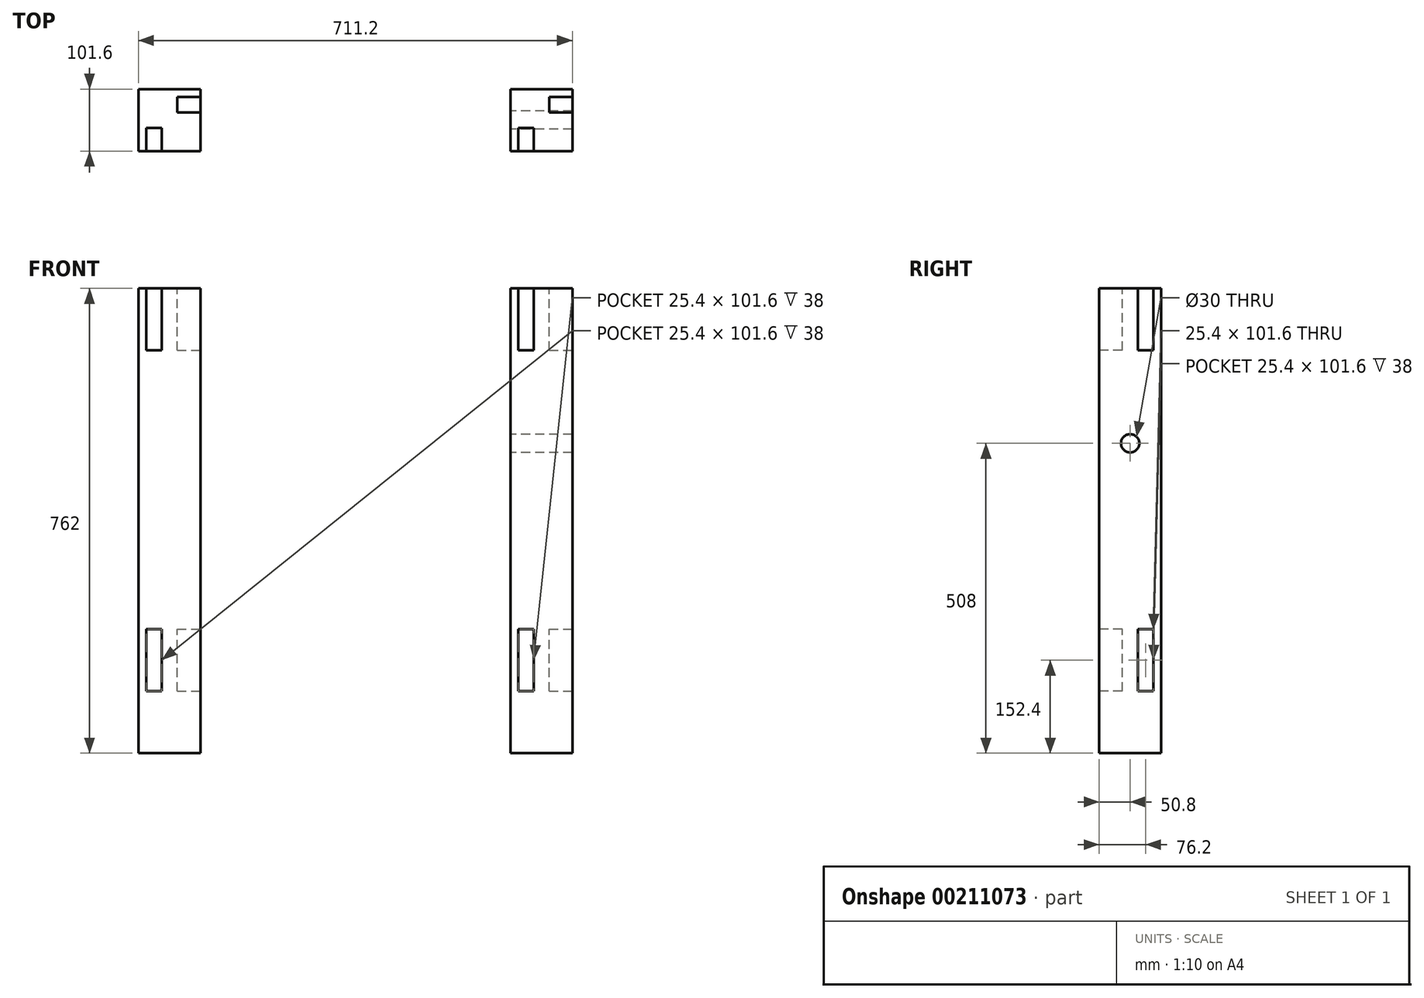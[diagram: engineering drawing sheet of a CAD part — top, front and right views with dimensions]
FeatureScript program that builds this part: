
annotation { "Feature Type Name" : "Feature", "Feature Type Description" : "" }
export const myFeature = defineFeature(function(context is Context, id is Id, definition is map)
    precondition{}
    {
        {
            var Q0;
            Q0=qCreatedBy(makeId("Top.planeOp"),FACE);
            var sketch = newSketch(context, id + "F0", { "sketchPlane" : qUnion([Q0])});
            skLineSegment(sketch, "E0.bottom", {"start": v(50.8, -50.8) * mm, "end": v(-50.8, -50.8) * mm});
            skLineSegment(sketch, "E0.top", {"start": v(50.8, 50.8) * mm, "end": v(-50.8, 50.8) * mm});
            skLineSegment(sketch, "E0.left", {"start": v(50.8, -50.8) * mm, "end": v(50.8, 50.8) * mm});
            skLineSegment(sketch, "E0.right", {"start": v(-50.8, -50.8) * mm, "end": v(-50.8, 50.8) * mm});
            skPoint(sketch, "E0.middle", {"position": v(0, 0) * mm});
            skSolve(sketch);
        }
        {
            var Q0;
            Q0=makeQuery(id+"F0.imprint","IMPRINT",FACE,{"disambiguationData":[TD([[makeQuery(id+"F0.imprint","IMPRINT",EDGE,{"derivedFrom":sQuery(id+"F0.wireOp",EDGE,"E0.bottom")}),-1.0]])]});
            extrude(context, id + "F1", {"entities" : qUnion([Q0]), "depth" : 762 * mm});
        }
        {
            var Q0;
            Q0=makeQuery(id+"F1.opExtrude","SWEPT_FACE",FACE,{"disambiguationData":[OSD([sQuery(id+"F0.wireOp",EDGE,"E0.bottom")])]});
            var sketch = newSketch(context, id + "F2", { "sketchPlane" : qUnion([Q0])});
            skLineSegment(sketch, "E1.bottom", {"start": v(-12.7, 101.6) * mm, "end": v(-38.1, 101.6) * mm});
            skLineSegment(sketch, "E1.top", {"start": v(-12.7, 203.2) * mm, "end": v(-38.1, 203.2) * mm});
            skLineSegment(sketch, "E1.left", {"start": v(-12.7, 101.6) * mm, "end": v(-12.7, 203.2) * mm});
            skLineSegment(sketch, "E1.right", {"start": v(-38.1, 101.6) * mm, "end": v(-38.1, 203.2) * mm});
            skPoint(sketch, "E1.middle", {"position": v(-25.4, 152.4) * mm});
            skLineSegment(sketch, "E2.top", {"start": v(-12.7, 762) * mm, "end": v(-38.1, 762) * mm});
            skLineSegment(sketch, "E2.left", {"start": v(-12.7, 660.4) * mm, "end": v(-12.7, 762) * mm});
            skLineSegment(sketch, "E2.right", {"start": v(-38.1, 660.4) * mm, "end": v(-38.1, 762) * mm});
            skPoint(sketch, "E2.middle", {"position": v(-25.4, 711.2) * mm});
            skLineSegment(sketch, "E3", {"start": v(-38.1, 660.4) * mm, "end": v(-12.7, 660.4) * mm});
            skSolve(sketch);
        }
        {
            var Q0;
            Q0=makeQuery(id+"F2.imprint","IMPRINT",FACE,{"disambiguationData":[TD([[makeQuery(id+"F2.imprint","IMPRINT",EDGE,{"derivedFrom":sQuery(id+"F2.wireOp",EDGE,"E1.bottom")}),-1.0]])]});
            var Q1;
            Q1=makeQuery(id+"F2.imprint","IMPRINT",FACE,{"disambiguationData":[TD([[makeQuery(id+"F2.imprint","IMPRINT",EDGE,{"derivedFrom":sQuery(id+"F2.wireOp",EDGE,"E2.top")}),1.0]])]});
            extrude(context, id + "F3", {"entities" : qUnion([Q0, Q1]), "operationType" : NewBodyOperationType.REMOVE, "oppositeDirection" : true, "depth" : 38 * mm});
        }
        {
            var Q0;
            Q0=makeQuery(id+"F1.opExtrude","SWEPT_FACE",FACE,{"disambiguationData":[OSD([sQuery(id+"F0.wireOp",EDGE,"E0.left")])]});
            var sketch = newSketch(context, id + "F4", { "sketchPlane" : qUnion([Q0])});
            skLineSegment(sketch, "E4.bottom", {"start": v(38.1, 101.6) * mm, "end": v(12.7, 101.6) * mm});
            skLineSegment(sketch, "E4.top", {"start": v(38.1, 203.2) * mm, "end": v(12.7, 203.2) * mm});
            skLineSegment(sketch, "E4.left", {"start": v(38.1, 101.6) * mm, "end": v(38.1, 203.2) * mm});
            skLineSegment(sketch, "E4.right", {"start": v(12.7, 101.6) * mm, "end": v(12.7, 203.2) * mm});
            skPoint(sketch, "E4.middle", {"position": v(25.4, 152.4) * mm});
            skLineSegment(sketch, "E5.bottom", {"start": v(38.1, 660.4) * mm, "end": v(12.7, 660.4) * mm});
            skLineSegment(sketch, "E5.top", {"start": v(38.1, 762) * mm, "end": v(12.7, 762) * mm});
            skLineSegment(sketch, "E5.left", {"start": v(38.1, 660.4) * mm, "end": v(38.1, 762) * mm});
            skLineSegment(sketch, "E5.right", {"start": v(12.7, 660.4) * mm, "end": v(12.7, 762) * mm});
            skPoint(sketch, "E5.middle", {"position": v(25.4, 711.2) * mm});
            skSolve(sketch);
        }
        {
            var Q0;
            Q0=makeQuery(id+"F4.imprint","IMPRINT",FACE,{"disambiguationData":[TD([[makeQuery(id+"F4.imprint","IMPRINT",EDGE,{"derivedFrom":sQuery(id+"F4.wireOp",EDGE,"E4.bottom")}),-1.0]])]});
            var Q1;
            Q1=makeQuery(id+"F4.imprint","IMPRINT",FACE,{"disambiguationData":[TD([[makeQuery(id+"F4.imprint","IMPRINT",EDGE,{"derivedFrom":sQuery(id+"F4.wireOp",EDGE,"E5.bottom")}),-1.0]])]});
            extrude(context, id + "F5", {"entities" : qUnion([Q0, Q1]), "operationType" : NewBodyOperationType.REMOVE, "oppositeDirection" : true, "depth" : 38 * mm});
        }
        {
            var Q0;
            Q0=makeQuery(id+"F1.opExtrude","SWEPT_BODY",BODY,{"disambiguationData":[OSD([sQuery(id+"F0.wireOp",EDGE,"E0.bottom"),sQuery(id+"F0.wireOp",EDGE,"E0.top"),sQuery(id+"F0.wireOp",EDGE,"E0.left"),sQuery(id+"F0.wireOp",EDGE,"E0.right")])]});
            transform(context, id + "F6", {"entities" : qUnion([Q0]), "transformType" : TransformType.TRANSLATION_3D, "dx" : 609.6 * mm, "dy" : 0 * mm, "dz" : 0 * mm, "makeCopy" : true});
        }
        {
            var Q0;
            Q0=makeQuery(id+"F6.opPattern","COPY",FACE,{"derivedFrom":makeQuery(id+"F1.opExtrude","SWEPT_FACE",FACE,{"disambiguationData":[OSD([sQuery(id+"F0.wireOp",EDGE,"E0.right")])]}),"instanceName":"1"});
            var sketch = newSketch(context, id + "F7", { "sketchPlane" : qUnion([Q0])});
            skCircle(sketch, "E6", {"center": v(0, 508) * mm, "radius": 15 * mm});
            skSolve(sketch);
        }
        {
            var Q0;
            Q0 = qSketchRegion(id + "F7", true);
            var Q1;
            Q1=makeQuery(id+"F6.opPattern","COPY",FACE,{"derivedFrom":makeQuery(id+"F1.opExtrude","SWEPT_FACE",FACE,{"disambiguationData":[OSD([sQuery(id+"F0.wireOp",EDGE,"E0.left")])]}),"instanceName":"1"});
            extrude(context, id + "F8", {"entities" : qUnion([Q0]), "operationType" : NewBodyOperationType.REMOVE, "endBound" : BoundingType.UP_TO_SURFACE, "oppositeDirection" : true, "endBoundEntityFace" : qUnion([Q1]), "depth" : 25.4 * mm});
        }
    });
